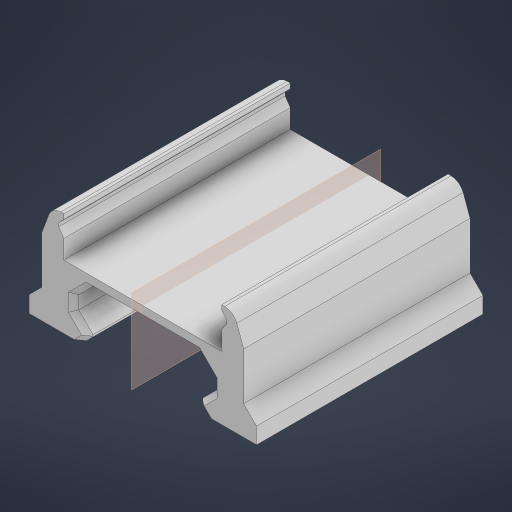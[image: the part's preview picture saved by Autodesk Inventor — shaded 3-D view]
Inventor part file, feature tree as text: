
AUTODESK INVENTOR PART (.ipt)
format: ipt  version: 2023 (Build 270158000, 158)  size: 347,136 bytes
history: native  units: in
note: dims shown in document units (in); Inventor stores cm internally (conversion verified against a paired STEP export)
features: other x4, extrude x3, chamfer x3, projected_geometry x3, sketch x2, reference x2, plane x1, mirror x1, fillet x1
ambient origin geometry x8: Origin, YZ Plane, XZ Plane, XY Plane, X Axis, Y Axis, Z Axis, Center Point
bodies: Solid1 (feature_tree)
feature tree (20):
  extrude  "Extrusion1"  Depth=0.1969in
  plane  "Work Plane2"
  chamfer  "Chamfer1"  Distance=0.1969in
  sketch  "Sketch3"  dims[d0=0.0039in d1=0.1969in]
  chamfer  "Chamfer2"  Distance=1.378in
  extrude  "Extrusion5"  Depth=0.0787in TaperAngle=45.0deg
  mirror  "Mirror3"
  fillet  "Fillet3"  Radius=0.0315in
  extrude  "Extrusion6"  Depth=0.0787in
  chamfer  "Chamfer4"  Distance=0.0787in
  reference  "Reference1"
  reference  "Reference3"
  projected_geometry  "Projected Loop1"
  projected_geometry  "Projected Loop3"
  sketch  "Sketch6"  dims[d2=0.0591in d5=0.1969in d6=1.378in d7=0.0in d8=0.0394in d9=0.125in d10=45.0deg d27=0.0315in d28=0.125in d29=45.0deg d44=0.1575in d45=0.0787in d46=0.0984in d48=0.0157in d49=0.0472in d50=0.481in d51=0.3937in d52=0.0in d53=0.0787in d54=0.0787in d55=0.0in d56=0.0in d57=0.0787in d58=0.0787in d59=45.0deg]
  projected_geometry  "Projected Loop4"
  parser-record x1  (decoder bookkeeping rows leaked as tree rows — omitted from the tree; the rows remain in map.json)
  other  "Rail assembly.iam"
  other  "Picatinny model:1"
  other  "IMU Module:1"
note: 1 file-system path scrubbed to <path> (originals preserved in map.json)
